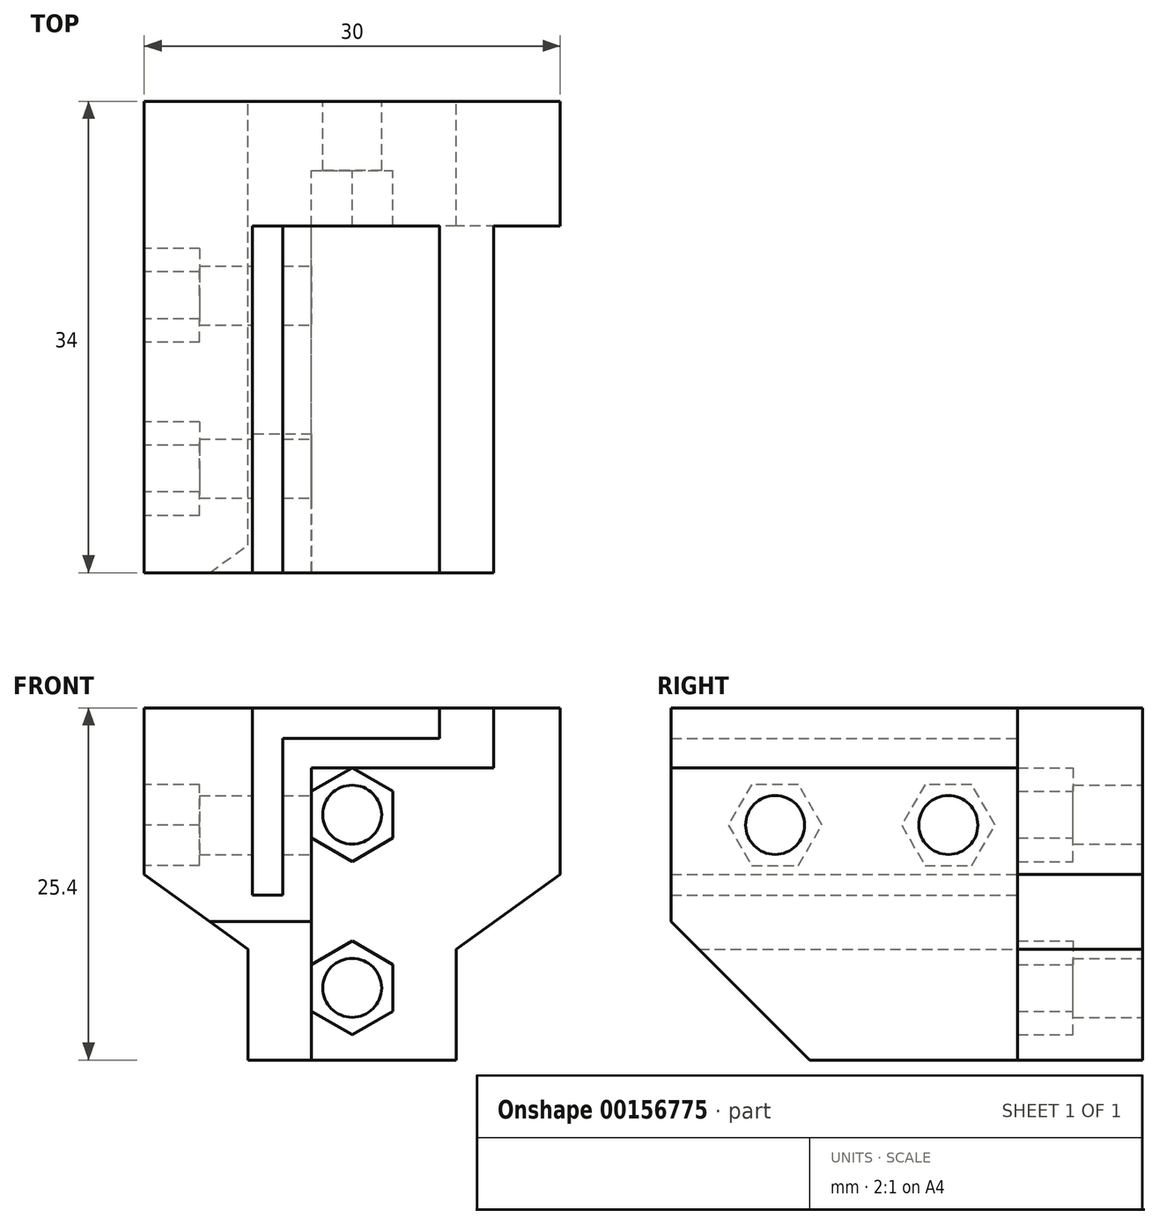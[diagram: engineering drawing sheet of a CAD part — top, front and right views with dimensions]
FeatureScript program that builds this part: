
annotation { "Feature Type Name" : "Feature", "Feature Type Description" : "" }
export const myFeature = defineFeature(function(context is Context, id is Id, definition is map)
    precondition{}
    {
        {
            var Q0;
            Q0=qCreatedBy(makeId("Front.planeOp"),FACE);
            var sketch = newSketch(context, id + "F0", { "sketchPlane" : qUnion([Q0])});
            skLineSegment(sketch, "E0.bottom", {"start": v(7.5, -12.7) * mm, "end": v(-7.5, -12.7) * mm});
            skLineSegment(sketch, "E0.top", {"start": v(15, 12.7) * mm, "end": v(-15, 12.7) * mm});
            skLineSegment(sketch, "E0.left", {"start": v(15, 0.7) * mm, "end": v(15, 12.7) * mm});
            skLineSegment(sketch, "E0.right", {"start": v(-15, 0.7) * mm, "end": v(-15, 12.7) * mm});
            skPoint(sketch, "E0.middle", {"position": v(0, 0) * mm});
            skCircle(sketch, "E1", {"center": v(0, 5) * mm, "radius": 2.12 * mm});
            skCircle(sketch, "E2", {"center": v(0, -7.5) * mm, "radius": 2.12 * mm});
            skLineSegment(sketch, "E3", {"start": v(-15, 0.7) * mm, "end": v(-7.5, -4.7) * mm});
            skLineSegment(sketch, "E4", {"start": v(-7.5, -4.7) * mm, "end": v(-7.5, -12.7) * mm});
            skLineSegment(sketch, "E5.MirrorCS", {"start": v(15, 0.7) * mm, "end": v(7.5, -4.7) * mm});
            skLineSegment(sketch, "E6.MirrorCS", {"start": v(7.5, -4.7) * mm, "end": v(7.5, -12.7) * mm});
            skPoint(sketch, "E7.orphan", {"position": v(-15, -12.7) * mm});
            skPoint(sketch, "E8.orphan", {"position": v(15, -12.7) * mm});
            skSolve(sketch);
        }
        {
            var Q0;
            Q0=qSketchRegion(id+"F0",true);
            extrude(context, id + "F1", {"entities" : qUnion([Q0]), "depth" : 5 * mm});
        }
        {
            var Q0;
            Q0=makeQuery(id+"F1.opExtrude","CAP_FACE",FACE,{"disambiguationData":[OSD([sQuery(id+"F0.wireOp",EDGE,"E0.bottom"),sQuery(id+"F0.wireOp",EDGE,"E0.top"),sQuery(id+"F0.wireOp",EDGE,"E0.left"),sQuery(id+"F0.wireOp",EDGE,"E0.right"),sQuery(id+"F0.wireOp",EDGE,"E1"),sQuery(id+"F0.wireOp",EDGE,"E2"),sQuery(id+"F0.wireOp",EDGE,"E3"),sQuery(id+"F0.wireOp",EDGE,"E4"),sQuery(id+"F0.wireOp",EDGE,"E5.MirrorCS"),sQuery(id+"F0.wireOp",EDGE,"E6.MirrorCS")])],"isStart":false});
            var sketch = newSketch(context, id + "F2", { "sketchPlane" : qUnion([Q0])});
            skCircle(sketch, "E9.cCircle", {"center": v(0, -7.5) * mm, "radius": 2.92 * mm, "construction": true});
            skLineSegment(sketch, "E9.0", {"start": v(2.93, -5.81) * mm, "end": v(2.92, -9.19) * mm});
            skLineSegment(sketch, "E9.1", {"start": v(2.92, -9.19) * mm, "end": v(0, -10.88) * mm});
            skLineSegment(sketch, "E9.2", {"start": v(0, -10.88) * mm, "end": v(-2.93, -9.19) * mm});
            skLineSegment(sketch, "E9.3", {"start": v(-2.93, -9.19) * mm, "end": v(-2.93, -5.81) * mm});
            skLineSegment(sketch, "E9.4", {"start": v(-2.92, -5.81) * mm, "end": v(0, -4.12) * mm});
            skLineSegment(sketch, "E9.5", {"start": v(0, -4.12) * mm, "end": v(2.93, -5.81) * mm});
            skPoint(sketch, "E9.0.midPoint", {"position": v(2.92, -7.5) * mm});
            skCircle(sketch, "E10.cCircle", {"center": v(0, 5) * mm, "radius": 2.93 * mm, "construction": true});
            skLineSegment(sketch, "E10.0", {"start": v(2.93, 6.69) * mm, "end": v(2.93, 3.31) * mm});
            skLineSegment(sketch, "E10.1", {"start": v(2.93, 3.31) * mm, "end": v(0, 1.62) * mm});
            skLineSegment(sketch, "E10.2", {"start": v(0, 1.62) * mm, "end": v(-2.93, 3.31) * mm});
            skLineSegment(sketch, "E10.3", {"start": v(-2.92, 3.31) * mm, "end": v(-2.92, 6.69) * mm});
            skLineSegment(sketch, "E10.4", {"start": v(-2.92, 6.69) * mm, "end": v(0, 8.38) * mm});
            skLineSegment(sketch, "E10.5", {"start": v(0, 8.38) * mm, "end": v(2.93, 6.69) * mm});
            skPoint(sketch, "E10.0.midPoint", {"position": v(2.93, 5) * mm});
            skLineSegment(sketch, "E11", {"start": v(-15, 12.7) * mm, "end": v(15, 12.7) * mm});
            skLineSegment(sketch, "E12", {"start": v(15, 12.7) * mm, "end": v(15, 0.7) * mm});
            skLineSegment(sketch, "E13", {"start": v(15, 0.7) * mm, "end": v(7.5, -4.7) * mm});
            skLineSegment(sketch, "E14", {"start": v(7.5, -4.7) * mm, "end": v(7.5, -12.7) * mm});
            skLineSegment(sketch, "E15", {"start": v(7.5, -12.7) * mm, "end": v(-7.5, -12.7) * mm});
            skLineSegment(sketch, "E16", {"start": v(-7.5, -12.7) * mm, "end": v(-7.5, -4.7) * mm});
            skLineSegment(sketch, "E17", {"start": v(-7.5, -4.7) * mm, "end": v(-15, 0.7) * mm});
            skLineSegment(sketch, "E18", {"start": v(-15, 0.7) * mm, "end": v(-15, 12.7) * mm});
            skSolve(sketch);
        }
        {
            var Q0;
            Q0 = qSketchRegion(id + "F2", true);
            extrude(context, id + "F3", {"entities" : qUnion([Q0]), "operationType" : NewBodyOperationType.ADD, "depth" : 4 * mm});
        }
        {
            var Q0;
            Q0=makeQuery(id+"F3.opExtrude","CAP_FACE",FACE,{"disambiguationData":[OSD([sQuery(id+"F2.wireOp",EDGE,"E9.0"),sQuery(id+"F2.wireOp",EDGE,"E9.1"),sQuery(id+"F2.wireOp",EDGE,"E9.2"),sQuery(id+"F2.wireOp",EDGE,"E9.3"),sQuery(id+"F2.wireOp",EDGE,"E9.4"),sQuery(id+"F2.wireOp",EDGE,"E9.5"),sQuery(id+"F2.wireOp",EDGE,"E10.0"),sQuery(id+"F2.wireOp",EDGE,"E10.1"),sQuery(id+"F2.wireOp",EDGE,"E10.2"),sQuery(id+"F2.wireOp",EDGE,"E10.3"),sQuery(id+"F2.wireOp",EDGE,"E10.4"),sQuery(id+"F2.wireOp",EDGE,"E10.5"),sQuery(id+"F2.wireOp",EDGE,"E11"),sQuery(id+"F2.wireOp",EDGE,"E12"),sQuery(id+"F2.wireOp",EDGE,"E13"),sQuery(id+"F2.wireOp",EDGE,"E14"),sQuery(id+"F2.wireOp",EDGE,"E15"),sQuery(id+"F2.wireOp",EDGE,"E16"),sQuery(id+"F2.wireOp",EDGE,"E17"),sQuery(id+"F2.wireOp",EDGE,"E18")])],"isStart":false});
            var sketch = newSketch(context, id + "F4", { "sketchPlane" : qUnion([Q0])});
            skLineSegment(sketch, "E19", {"start": v(-7.2, 12.7) * mm, "end": v(-7.2, -0.8) * mm});
            skLineSegment(sketch, "E20", {"start": v(-7.2, -0.8) * mm, "end": v(-5, -0.8) * mm});
            skLineSegment(sketch, "E21", {"start": v(-5, -0.8) * mm, "end": v(-5, 10.5) * mm});
            skLineSegment(sketch, "E22", {"start": v(-5, 10.5) * mm, "end": v(6.3, 10.5) * mm});
            skLineSegment(sketch, "E23", {"start": v(6.3, 10.5) * mm, "end": v(6.3, 12.7) * mm});
            skLineSegment(sketch, "E24", {"start": v(6.3, 12.7) * mm, "end": v(-7.2, 12.7) * mm, "construction": true});
            skLineSegment(sketch, "E25", {"start": v(-7.2, 12.7) * mm, "end": v(-15, 12.7) * mm});
            skLineSegment(sketch, "E26", {"start": v(-15, 12.7) * mm, "end": v(-15, 0.7) * mm});
            skLineSegment(sketch, "E27", {"start": v(-15, 0.7) * mm, "end": v(-7.5, -4.7) * mm});
            skLineSegment(sketch, "E28", {"start": v(10.2, 12.7) * mm, "end": v(6.3, 12.7) * mm});
            skLineSegment(sketch, "E29", {"start": v(-2.92, 3.31) * mm, "end": v(-2.92, 6.69) * mm});
            skLineSegment(sketch, "E30", {"start": v(10.2, 8.38) * mm, "end": v(10.2, 12.7) * mm});
            skLineSegment(sketch, "E31", {"start": v(-2.92, -12.7) * mm, "end": v(-2.92, 3.31) * mm});
            skLineSegment(sketch, "E32", {"start": v(-2.92, 8.38) * mm, "end": v(-2.92, 6.69) * mm});
            skLineSegment(sketch, "E33", {"start": v(-2.92, 8.38) * mm, "end": v(10.2, 8.38) * mm});
            skLineSegment(sketch, "E34", {"start": v(-7.5, -4.7) * mm, "end": v(-7.5, -12.7) * mm});
            skLineSegment(sketch, "E35", {"start": v(-7.5, -12.7) * mm, "end": v(-2.92, -12.7) * mm});
            skSolve(sketch);
        }
        {
            var Q0;
            Q0 = qSketchRegion(id + "F4", true);
            extrude(context, id + "F5", {"entities" : qUnion([Q0]), "operationType" : NewBodyOperationType.ADD, "depth" : 25 * mm});
        }
        {
            var Q0;
            Q0=makeQuery(id+"F5.boolean.opBoolean","MERGE",FACE,{"derivedFrom":[makeQuery(id+"F3.opExtrude","SWEPT_FACE",FACE,{"disambiguationData":[OSD([sQuery(id+"F2.wireOp",EDGE,"E10.3")])]}),makeQuery(id+"F5.opExtrude","SWEPT_FACE",FACE,{"disambiguationData":[OSD([sQuery(id+"F4.wireOp",EDGE,"E29"),sQuery(id+"F4.wireOp",EDGE,"E31"),sQuery(id+"F4.wireOp",EDGE,"E32")])]})]});
            var sketch = newSketch(context, id + "F6", { "sketchPlane" : qUnion([Q0])});
            skCircle(sketch, "E36", {"center": v(-26.5, 4.25) * mm, "radius": 2.12 * mm});
            skCircle(sketch, "E37", {"center": v(-14, 4.25) * mm, "radius": 2.12 * mm});
            skSolve(sketch);
        }
        {
            var Q0;
            Q0 = qSketchRegion(id + "F6", true);
            extrude(context, id + "F7", {"entities" : qUnion([Q0]), "operationType" : NewBodyOperationType.REMOVE, "oppositeDirection" : true, "depth" : 25 * mm});
        }
        {
            var Q0;
            Q0=makeQuery(id+"F5.boolean.opBoolean","MERGE",FACE,{"derivedFrom":[makeQuery(id+"F3.boolean.opBoolean","MERGE",FACE,{"derivedFrom":[makeQuery(id+"F1.opExtrude","SWEPT_FACE",FACE,{"disambiguationData":[OSD([sQuery(id+"F0.wireOp",EDGE,"E0.right")])]}),makeQuery(id+"F3.opExtrude","SWEPT_FACE",FACE,{"disambiguationData":[OSD([sQuery(id+"F2.wireOp",EDGE,"E18")])]})]}),makeQuery(id+"F5.opExtrude","SWEPT_FACE",FACE,{"disambiguationData":[OSD([sQuery(id+"F4.wireOp",EDGE,"E26")])]})]});
            var sketch = newSketch(context, id + "F8", { "sketchPlane" : qUnion([Q0])});
            skCircle(sketch, "E38.cCircle", {"center": v(14, 4.25) * mm, "radius": 2.93 * mm, "construction": true});
            skLineSegment(sketch, "E38.0", {"start": v(12.31, 7.17) * mm, "end": v(15.69, 7.17) * mm});
            skLineSegment(sketch, "E38.1", {"start": v(15.69, 7.17) * mm, "end": v(17.38, 4.25) * mm});
            skLineSegment(sketch, "E38.2", {"start": v(17.38, 4.25) * mm, "end": v(15.69, 1.32) * mm});
            skLineSegment(sketch, "E38.3", {"start": v(15.69, 1.32) * mm, "end": v(12.31, 1.32) * mm});
            skLineSegment(sketch, "E38.4", {"start": v(12.31, 1.33) * mm, "end": v(10.62, 4.25) * mm});
            skLineSegment(sketch, "E38.5", {"start": v(10.62, 4.25) * mm, "end": v(12.31, 7.17) * mm});
            skPoint(sketch, "E38.0.midPoint", {"position": v(14, 7.17) * mm});
            skCircle(sketch, "E39.cCircle", {"center": v(26.5, 4.25) * mm, "radius": 2.93 * mm, "construction": true});
            skLineSegment(sketch, "E39.0", {"start": v(24.81, 7.17) * mm, "end": v(28.19, 7.17) * mm});
            skLineSegment(sketch, "E39.1", {"start": v(28.19, 7.17) * mm, "end": v(29.88, 4.25) * mm});
            skLineSegment(sketch, "E39.2", {"start": v(29.88, 4.25) * mm, "end": v(28.19, 1.32) * mm});
            skLineSegment(sketch, "E39.3", {"start": v(28.19, 1.32) * mm, "end": v(24.81, 1.32) * mm});
            skLineSegment(sketch, "E39.4", {"start": v(24.81, 1.32) * mm, "end": v(23.12, 4.25) * mm});
            skLineSegment(sketch, "E39.5", {"start": v(23.12, 4.25) * mm, "end": v(24.81, 7.17) * mm});
            skPoint(sketch, "E39.0.midPoint", {"position": v(26.5, 7.17) * mm});
            skSolve(sketch);
        }
        {
            var Q0;
            Q0 = qSketchRegion(id + "F8", true);
            extrude(context, id + "F9", {"entities" : qUnion([Q0]), "operationType" : NewBodyOperationType.REMOVE, "oppositeDirection" : true, "depth" : 4 * mm});
        }
        {
            var Q0;
            Q0=makeQuery(id+"F5.opExtrude","CAP_EDGE",EDGE,{"disambiguationData":[OSD([sQuery(id+"F4.wireOp",EDGE,"E35")])],"isStart":false});
            chamfer(context, id + "F10", {"entities" : qUnion([Q0]), "width" : 10 * mm, "tangentPropagation" : true});
        }
    });
